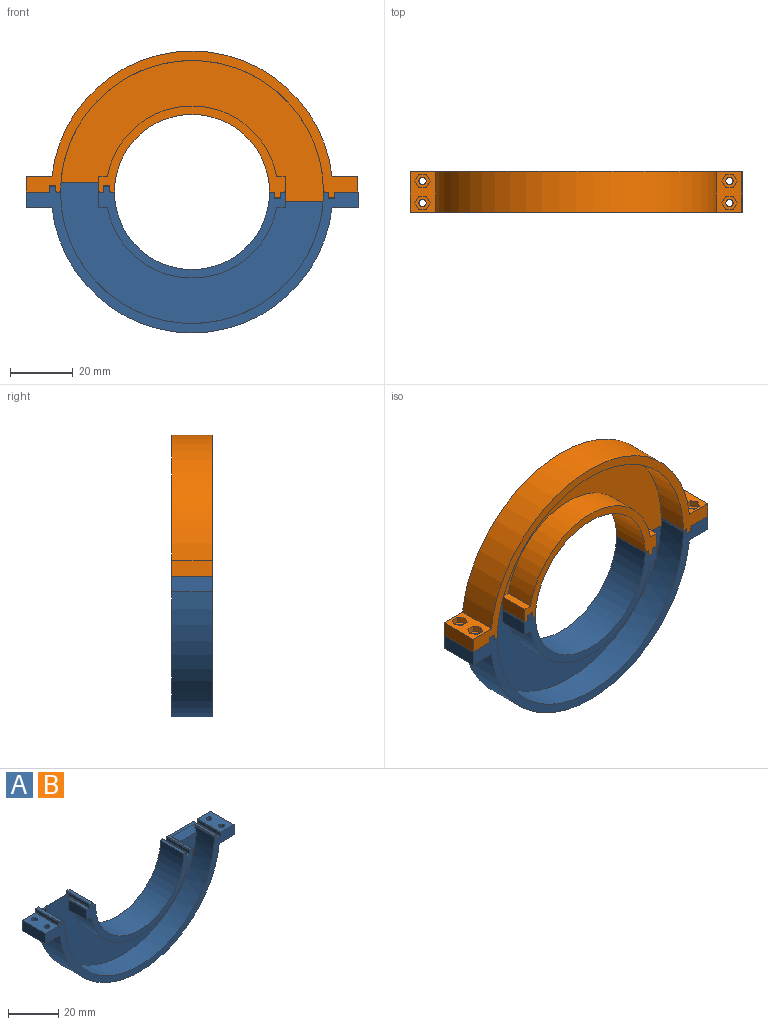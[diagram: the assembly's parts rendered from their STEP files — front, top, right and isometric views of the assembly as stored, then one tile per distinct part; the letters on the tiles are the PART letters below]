
ASSEMBLY  parts=2 mates=1
PART A: 91 faces, bbox 106x13x48 mm
  f0: plane 13x8.27mm, normal (0,0,-1), area 77mm2, adj f9,f13,f19,f21,f77,f78,f79,f80
  f1: cylinder r=1.15mm len=3mm, axis (0,0,1), area 21.7mm2, adj f17,f90
  f2: cylinder r=1.15mm len=3mm, axis (0,0,1), area 21.7mm2, adj f17,f83
  f3: plane 13x8.28mm, normal (0,0,-1), area 77.1mm2, adj f9,f13,f19,f31,f63,f64,f65,f66
  f4: cylinder r=1.15mm len=3mm, axis (0,0,1), area 21.7mm2, adj f8,f76
  f5: cylinder r=1.15mm len=3mm, axis (0,0,1), area 21.7mm2, adj f8,f69
  f6: plane 15.05x13mm, normal (0,0,1), area 50.8mm2, adj f11,f13,f14,f19,f40,f41,f42,f43
  f7: cylinder r=27.5mm len=54.08mm, axis (0,1,0), area 763.4mm2, adj f11,f14,f26,f35
  f8: plane 13x7.4mm, normal (0,0,1), area 87.9mm2, adj f4,f5,f13,f19,f31,f49
  f9: cylinder r=45mm len=89.44mm, axis (0,1,0), area 1707.6mm2, adj f0,f3,f13,f19
  f10: plane 13x1.3mm, normal (0,0,1), area 16.8mm2, adj f11,f18,f19,f53
  f11: plane 59.5x29.4mm, normal (0,-1,0), area 249.1mm2, adj f6,f7,f10,f12,f16,f18,f25,f26
  f12: plane 14.85x13mm, normal (0,0,1), area 46.3mm2, adj f11,f13,f19,f30,f52,f56,f58,f61
  f13: plane 106x46.9mm, normal (0,-1,0), area 490.3mm2, adj f0,f3,f6,f8,f9,f12,f15,f17
  f14: plane 84.09x45mm, normal (0,-1,0), area 1559.1mm2, adj f6,f7,f15,f25,f26,f30,f35,f36
  f15: cylinder r=42mm len=84mm, axis (0,1,0), area 1312.9mm2, adj f13,f14,f20,f30,f62
  f16: plane 13x1.4mm, normal (0,0,1), area 18.2mm2, adj f11,f18,f19,f44
  f17: plane 13x7.3mm, normal (0,0,1), area 86.6mm2, adj f1,f2,f13,f19,f21,f57
  f18: cylinder r=24.75mm len=49.5mm, axis (0,1,0), area 1010.8mm2, adj f10,f11,f16,f19
  f19: plane 106x46.9mm, normal (0,1,0), area 2298.4mm2, adj f0,f3,f6,f8,f9,f10,f12,f16
  f20: plane 11.49x0.41mm, normal (-1,0,0), area 4.7mm2, adj f13,f15,f30,f61
  f21: plane 13x5mm, normal (1,0,0), area 65mm2, adj f0,f13,f17,f19
  f22: plane 13x1.6mm, normal (1,0,0), area 20.8mm2, adj f13,f19,f58,f60
  f23: plane 13x1.6mm, normal (-1,0,0), area 20.8mm2, adj f13,f19,f57,f59
  f24: plane 13x1.6mm, normal (0,0,1), area 20.8mm2, adj f13,f19,f59,f60
  f25: plane 11.49x4.8mm, normal (1,0,0), area 50.1mm2, adj f11,f14,f26,f30,f56
  f26: plane 10x2.7mm, normal (0,0,-1), area 27mm2, adj f7,f11,f14,f25
  f27: plane 13x1.6mm, normal (1,0,0), area 20.8mm2, adj f11,f19,f53,f55
  f28: plane 13x1.6mm, normal (-1,0,0), area 20.8mm2, adj f11,f19,f52,f54
  f29: plane 13x1.6mm, normal (0,0,1), area 20.8mm2, adj f11,f19,f54,f55
  f30: plane 12.65x3mm, normal (0,-0.88,0.47), area 41.6mm2, adj f12,f14,f15,f20,f25,f56,f61
  f31: plane 13x5mm, normal (-1,0,0), area 65mm2, adj f3,f8,f13,f19
  f32: plane 13x1.5mm, normal (1,0,0), area 19.5mm2, adj f13,f19,f48,f50
  f33: plane 13x1.5mm, normal (-1,0,0), area 19.5mm2, adj f13,f19,f49,f51
  f34: plane 13x1.4mm, normal (0,0,1), area 18.2mm2, adj f13,f19,f50,f51
  f35: plane 10x2.71mm, normal (0,0,-1), area 27.1mm2, adj f7,f11,f14,f36
  f36: plane 10x4.8mm, normal (-1,0,0), area 48mm2, adj f11,f14,f35,f47
  f37: plane 13x1.5mm, normal (1,0,0), area 19.5mm2, adj f11,f19,f44,f46
  f38: plane 13x1.5mm, normal (-1,0,0), area 19.5mm2, adj f11,f19,f43,f45
  f39: plane 13x1.4mm, normal (0,0,1), area 18.2mm2, adj f11,f19,f45,f46
  f40: plane 3x1.5mm, normal (1,0,0), area 2.3mm2, adj f6,f14,f42
  f41: plane 3x1.5mm, normal (-1,0,0), area 2.2mm2, adj f6,f14,f42
  f42: plane 12.25x3mm, normal (0,0.89,0.45), area 41.1mm2, adj f6,f14,f40,f41
  f43: cylinder r=0.2mm len=13mm, axis (0,-1,0), area 4.1mm2, adj f6,f11,f19,f38
  f44: cylinder r=0.2mm len=13mm, axis (0,1,0), area 4.1mm2, adj f11,f16,f19,f37
  f45: cylinder r=0.2mm len=13mm, axis (0,1,0), area 4.1mm2, adj f11,f19,f38,f39
  f46: cylinder r=0.2mm len=13mm, axis (0,-1,0), area 4.1mm2, adj f11,f19,f37,f39
  f47: cylinder r=0.2mm len=10mm, axis (0,-1,0), area 3.1mm2, adj f6,f11,f14,f36
  f48: cylinder r=0.2mm len=13mm, axis (0,1,0), area 4.1mm2, adj f6,f13,f19,f32
  f49: cylinder r=0.2mm len=13mm, axis (0,-1,0), area 4.1mm2, adj f8,f13,f19,f33
  f50: cylinder r=0.2mm len=13mm, axis (0,-1,0), area 4.1mm2, adj f13,f19,f32,f34
  f51: cylinder r=0.2mm len=13mm, axis (0,1,0), area 4.1mm2, adj f13,f19,f33,f34
  f52: cylinder r=0.2mm len=13mm, axis (0,-1,0), area 4.1mm2, adj f11,f12,f19,f28
  f53: cylinder r=0.2mm len=13mm, axis (0,1,0), area 4.1mm2, adj f10,f11,f19,f27
  f54: cylinder r=0.2mm len=13mm, axis (0,1,0), area 4.1mm2, adj f11,f19,f28,f29
  f55: cylinder r=0.2mm len=13mm, axis (0,-1,0), area 4.1mm2, adj f11,f19,f27,f29
  f56: cylinder r=0.2mm len=11.6mm, axis (0,1,0), area 3.6mm2, adj f11,f12,f25,f30
  f57: cylinder r=0.2mm len=13mm, axis (0,-1,0), area 4.1mm2, adj f13,f17,f19,f23
  f58: cylinder r=0.2mm len=13mm, axis (0,1,0), area 4.1mm2, adj f12,f13,f19,f22
  f59: cylinder r=0.2mm len=13mm, axis (0,1,0), area 4.1mm2, adj f13,f19,f23,f24
  f60: cylinder r=0.2mm len=13mm, axis (0,-1,0), area 4.1mm2, adj f13,f19,f22,f24
  f61: cylinder r=0.2mm len=11.6mm, axis (0,-1,0), area 3.6mm2, adj f12,f13,f20,f30
  f62: cylinder r=0.2mm len=10mm, axis (0,1,0), area 3.1mm2, adj f6,f13,f14,f15
  f63: plane 2.43x2mm, normal (0,1,0), area 4.8mm2, adj f3,f64,f68,f69
  f64: plane 2.1x2mm, normal (0.87,0.5,0), area 4.8mm2, adj f3,f63,f65,f69
  f65: plane 2.1x2mm, normal (0.87,-0.5,0), area 4.8mm2, adj f3,f64,f66,f69
  f66: plane 2.43x2mm, normal (0,-1,0), area 4.8mm2, adj f3,f65,f67,f69
  f67: plane 2.1x2mm, normal (-0.87,-0.5,0), area 4.8mm2, adj f3,f66,f68,f69
  f68: plane 2.1x2mm, normal (-0.87,0.5,0), area 4.8mm2, adj f3,f63,f67,f69
  f69: plane 4.85x4.2mm, normal (0,0,-1), area 11.1mm2, adj f5,f63,f64,f65,f66,f67,f68
  f70: plane 2.43x2mm, normal (0,1,0), area 4.8mm2, adj f3,f71,f75,f76
  f71: plane 2.1x2mm, normal (0.87,0.5,0), area 4.8mm2, adj f3,f70,f72,f76
  f72: plane 2.1x2mm, normal (0.87,-0.5,0), area 4.8mm2, adj f3,f71,f73,f76
  f73: plane 2.43x2mm, normal (0,-1,0), area 4.8mm2, adj f3,f72,f74,f76
  f74: plane 2.1x2mm, normal (-0.87,-0.5,0), area 4.8mm2, adj f3,f73,f75,f76
  f75: plane 2.1x2mm, normal (-0.87,0.5,0), area 4.8mm2, adj f3,f70,f74,f76
  f76: plane 4.85x4.2mm, normal (0,0,-1), area 11.1mm2, adj f4,f70,f71,f72,f73,f74,f75
  f77: plane 2.43x2mm, normal (0,1,0), area 4.8mm2, adj f0,f78,f82,f83
  f78: plane 2.1x2mm, normal (0.87,0.5,0), area 4.8mm2, adj f0,f77,f79,f83
  f79: plane 2.1x2mm, normal (0.87,-0.5,0), area 4.8mm2, adj f0,f78,f80,f83
  f80: plane 2.43x2mm, normal (0,-1,0), area 4.8mm2, adj f0,f79,f81,f83
  f81: plane 2.1x2mm, normal (-0.87,-0.5,0), area 4.8mm2, adj f0,f80,f82,f83
  f82: plane 2.1x2mm, normal (-0.87,0.5,0), area 4.8mm2, adj f0,f77,f81,f83
  f83: plane 4.85x4.2mm, normal (0,0,-1), area 11.1mm2, adj f2,f77,f78,f79,f80,f81,f82
  f84: plane 2.43x2mm, normal (0,1,0), area 4.8mm2, adj f0,f85,f89,f90
  f85: plane 2.1x2mm, normal (0.87,0.5,0), area 4.8mm2, adj f0,f84,f86,f90
  f86: plane 2.1x2mm, normal (0.87,-0.5,0), area 4.8mm2, adj f0,f85,f87,f90
  f87: plane 2.43x2mm, normal (0,-1,0), area 4.8mm2, adj f0,f86,f88,f90
  f88: plane 2.1x2mm, normal (-0.87,-0.5,0), area 4.8mm2, adj f0,f87,f89,f90
  f89: plane 2.1x2mm, normal (-0.87,0.5,0), area 4.8mm2, adj f0,f84,f88,f90
  f90: plane 4.85x4.2mm, normal (0,0,-1), area 11.1mm2, adj f1,f84,f85,f86,f87,f88,f89
PART B: same geometry as A
PLACE A t=(-25.59,-36.6,-18.69)mm
PLACE B rot(axis=(0,1,0),180deg) t=(-25.6,-36.6,-18.69)mm
MATE fastened B.f1 <-> A.f4  axis (0,0,-1) through (-74.59,-46.6,-18.69)mm
